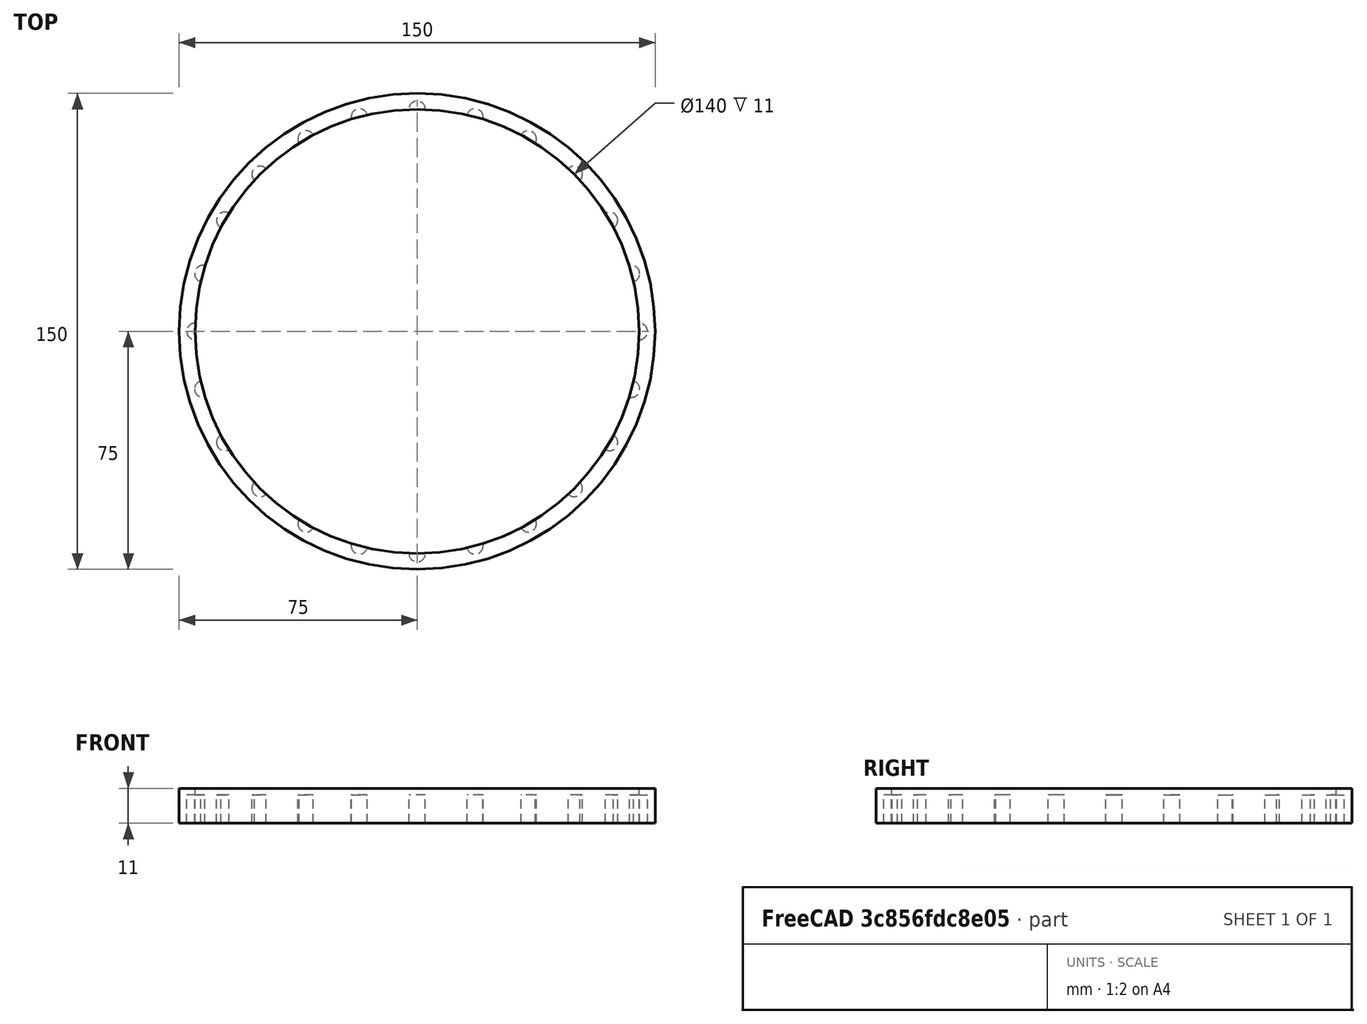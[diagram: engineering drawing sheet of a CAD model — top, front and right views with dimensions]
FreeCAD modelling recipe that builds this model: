
FCSTD DOCUMENT
Label: rat.social.top.outside
objects: Part::Cylinder×9, Part::Mirroring×3, Part::Cut×2, Part::MultiFuse×2
note: 16 computed .brp shape members not serialized (recipe doc carries the construction recipe); baked Part::Feature solids carry a one-line shape summary decoded from their .brp

FEATURE [Part::Cylinder] Cylinder
  Angle = 360
  Height = 20
  Radius = 70
FEATURE [Part::Cylinder] Cylinder001  label="pole1"
  Angle = 360
  Height = 9
  Placement = pos=(70,0,0) rot=(0,0,1;0rad)
  Radius = 2.6
FEATURE [Part::Cylinder] Cylinder002
  Angle = 360
  Height = 11
  Radius = 75
FEATURE [Part::Cylinder] Cylinder001001  label="pole0"
  Angle = 360
  Height = 9
  Placement = pos=(0,70,0) rot=(0,0,1;0rad)
  Radius = 2.6
FEATURE [Part::Cylinder] Cylinder001002  label="pole006"
  Angle = 360
  Height = 9
  Placement = pos=(18.2,67.55,0) rot=(0,0,1;0rad)
  Radius = 2.6
FEATURE [Part::Cylinder] Cylinder001002001  label="pole2"
  Angle = 360
  Height = 9
  Placement = pos=(67.55,18.2,0) rot=(0,0,1;0rad)
  Radius = 2.6
FEATURE [Part::Cylinder] Cylinder001002001001  label="pole003"
  Angle = 360
  Height = 9
  Placement = pos=(60.62,35,0) rot=(0,0,1;0rad)
  Radius = 2.6
FEATURE [Part::Cylinder] Cylinder001002001001001  label="pole004"
  Angle = 360
  Height = 9
  Placement = pos=(49.49,49.49,0) rot=(0,0,1;0rad)
  Radius = 2.6
FEATURE [Part::Cylinder] Cylinder001002001001001001  label="pole005"
  Angle = 360
  Height = 9
  Placement = pos=(35,60.62,0) rot=(0,0,1;0rad)
  Radius = 2.6
FEATURE [Part::Cut] Cut
  Base = -> Cylinder002
  Tool = -> Cylinder
FEATURE [Part::MultiFuse] Fusion
  Shapes = -> [Cylinder001001,Cylinder001,Cylinder001002001,Cylinder001002001001,Cylinder001002001001001,Cylinder001002001001001001,Cylinder001002]
FEATURE [Part::Mirroring] Part__Mirroring  label="Fusion (Mirror #1)"
  Base = (0,0,0)
  Normal = (0,1,0)
  Source = -> Fusion
FEATURE [Part::Mirroring] Part__Mirroring001  label="Fusion (Mirror #2)"
  Base = (0,0,0)
  Normal = (1,0,0)
  Source = -> Part__Mirroring
FEATURE [Part::Mirroring] Part__Mirroring002  label="Fusion (Mirror #3)"
  Base = (0,0,0)
  Normal = (0,1,0)
  Source = -> Part__Mirroring001
FEATURE [Part::MultiFuse] Fusion001
  Shapes = -> [Fusion,Part__Mirroring,Part__Mirroring001,Part__Mirroring002]
FEATURE [Part::Cut] Cut001
  Base = -> Cut
  Tool = -> Fusion001
